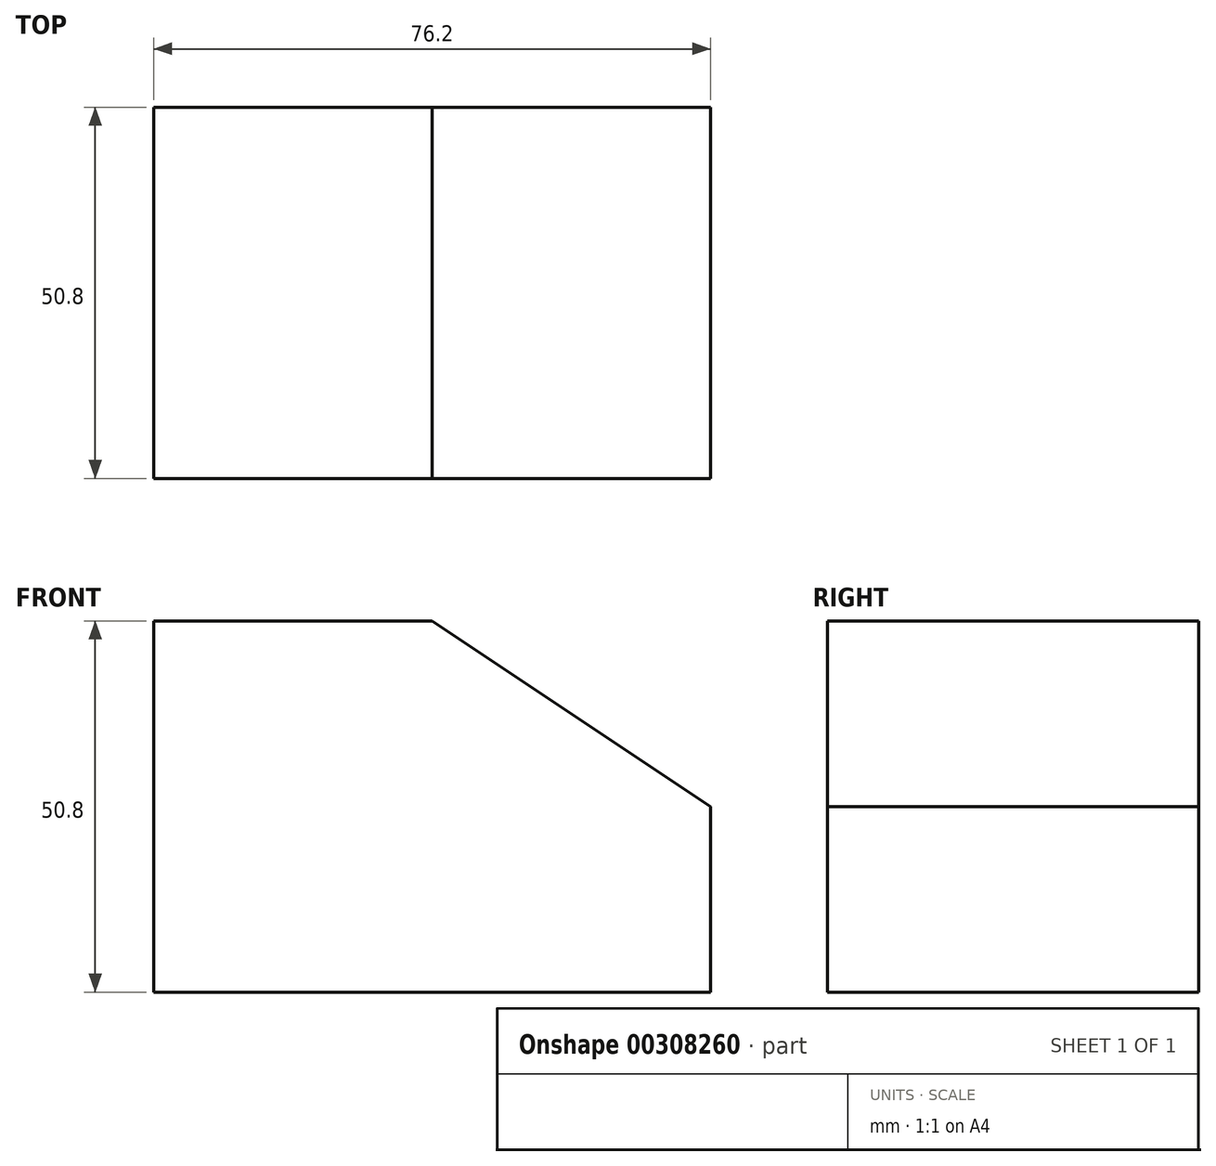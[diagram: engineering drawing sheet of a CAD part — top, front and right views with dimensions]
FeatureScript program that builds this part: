
annotation { "Feature Type Name" : "Feature", "Feature Type Description" : "" }
export const myFeature = defineFeature(function(context is Context, id is Id, definition is map)
    precondition{}
    {
        {
            var Q0;
            Q0=qCreatedBy(makeId("Front.planeOp"),FACE);
            var sketch = newSketch(context, id + "F0", { "sketchPlane" : qUnion([Q0])});
            skLineSegment(sketch, "E0", {"start": v(-38.1, -29.01) * mm, "end": v(38.1, -29.01) * mm});
            skLineSegment(sketch, "E1", {"start": v(-38.1, -29.01) * mm, "end": v(-38.1, 21.79) * mm});
            skLineSegment(sketch, "E2", {"start": v(-38.1, 21.79) * mm, "end": v(0, 21.79) * mm});
            skLineSegment(sketch, "E3", {"start": v(38.1, -29.01) * mm, "end": v(38.1, -3.61) * mm});
            skLineSegment(sketch, "E4", {"start": v(38.1, -3.61) * mm, "end": v(0, 21.79) * mm});
            skSolve(sketch);
        }
        {
            var Q0;
            Q0 = qSketchRegion(id + "F0", true);
            extrude(context, id + "F1", {"entities" : qUnion([Q0]), "depth" : 50.8 * mm});
        }
    });
